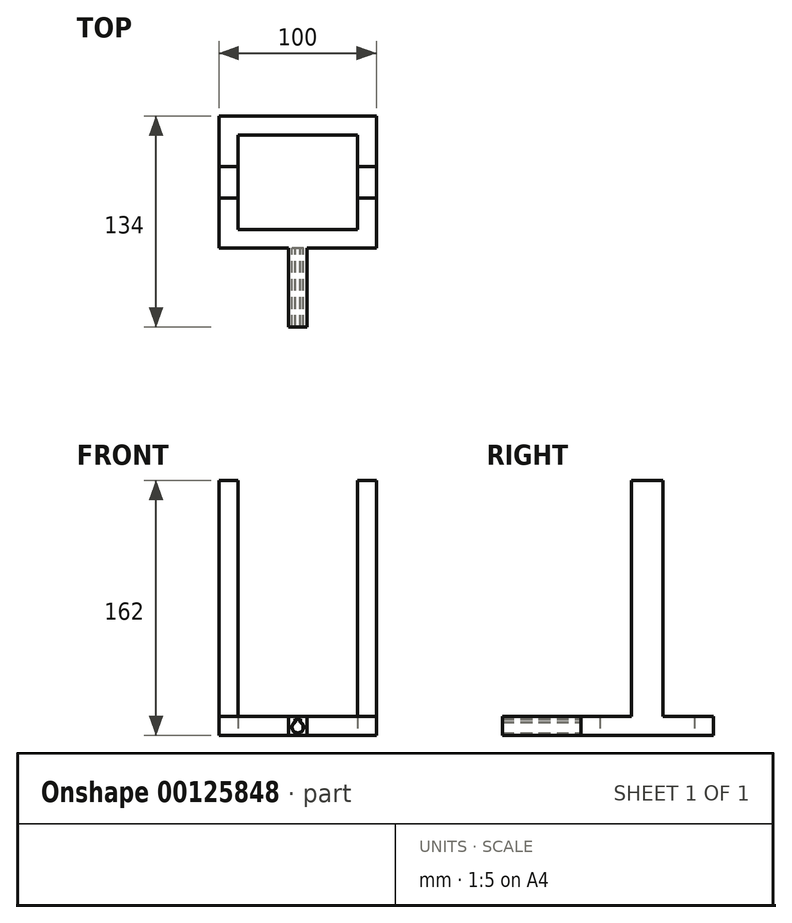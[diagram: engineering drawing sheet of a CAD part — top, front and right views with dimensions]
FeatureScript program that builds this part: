
annotation { "Feature Type Name" : "Feature", "Feature Type Description" : "" }
export const myFeature = defineFeature(function(context is Context, id is Id, definition is map)
    precondition{}
    {
        {
            var Q0;
            Q0=qCreatedBy(makeId("Front.planeOp"),FACE);
            var sketch = newSketch(context, id + "F12", { "sketchPlane" : qUnion([Q0])});
            skCircle(sketch, "E0", {"center": v(0, 0) * mm, "radius": 3.5 * mm});
            skPoint(sketch, "E1", {"position": v(0, 3.5) * mm});
            skSolve(sketch);
        }
        {
            var Q0;
            Q0=makeQuery(id+"F12.imprint","IMPRINT",FACE,{"disambiguationData":[TD([[makeQuery(id+"F12.imprint","IMPRINT",EDGE,{"derivedFrom":sQuery(id+"F12.wireOp",EDGE,"E0")}),1.0]])]});
            extrude(context, id + "F0", {"entities" : qUnion([Q0]), "depth" : 50 * mm});
        }
        {
            var Q0;
            Q0=qCreatedBy(makeId("Front.planeOp"),FACE);
            var sketch = newSketch(context, id + "F13", { "sketchPlane" : qUnion([Q0])});
            skPoint(sketch, "E2", {"position": v(0, 3.5) * mm});
            skLineSegment(sketch, "E3.bottom", {"start": v(1.5, 5) * mm, "end": v(-1.5, 5) * mm});
            skLineSegment(sketch, "E3.top", {"start": v(1.5, 2) * mm, "end": v(-1.5, 2) * mm});
            skLineSegment(sketch, "E3.left", {"start": v(1.5, 5) * mm, "end": v(1.5, 2) * mm});
            skLineSegment(sketch, "E3.right", {"start": v(-1.5, 5) * mm, "end": v(-1.5, 2) * mm});
            skSolve(sketch);
        }
        {
            var Q0;
            Q0=qSketchRegion(id+"F13",true);
            extrude(context, id + "F1", {"entities" : qUnion([Q0]), "operationType" : NewBodyOperationType.ADD, "depth" : 50 * mm});
        }
        {
            var Q0;
            Q0=makeQuery(id+"F1.boolean.opBoolean","MERGE",FACE,{"derivedFrom":[makeQuery(id+"F0.opExtrude","CAP_FACE",FACE,{"disambiguationData":[OSD([sQuery(id+"F12.wireOp",EDGE,"E0")])],"isStart":false}),makeQuery(id+"F1.opExtrude","CAP_FACE",FACE,{"disambiguationData":[OSD([sQuery(id+"F13.wireOp",EDGE,"E3.bottom"),sQuery(id+"F13.wireOp",EDGE,"E3.top"),sQuery(id+"F13.wireOp",EDGE,"E3.left"),sQuery(id+"F13.wireOp",EDGE,"E3.right")])],"isStart":false})]});
            var sketch = newSketch(context, id + "F14", { "sketchPlane" : qUnion([Q0])});
            skPoint(sketch, "E4", {"position": v(0, -3.5) * mm});
            skPoint(sketch, "E5", {"position": v(0, 5) * mm});
            skPoint(sketch, "E6", {"position": v(0, 0.75) * mm});
            skSolve(sketch);
        }
        {
            var Q0;
            Q0=qCreatedBy(makeId("Front.planeOp"),FACE);
            var sketch = newSketch(context, id + "F15", { "sketchPlane" : qUnion([Q0])});
            skPoint(sketch, "E7", {"position": v(0, 0.75) * mm});
            skLineSegment(sketch, "E8.bottom", {"start": v(6, -5.25) * mm, "end": v(-6, -5.25) * mm});
            skLineSegment(sketch, "E8.top", {"start": v(6, 6.75) * mm, "end": v(-6, 6.75) * mm});
            skLineSegment(sketch, "E8.left", {"start": v(6, -5.25) * mm, "end": v(6, 6.75) * mm});
            skLineSegment(sketch, "E8.right", {"start": v(-6, -5.25) * mm, "end": v(-6, 6.75) * mm});
            skSolve(sketch);
        }
        {
            var Q0;
            Q0=qSketchRegion(id+"F15",true);
            extrude(context, id + "F2", {"entities" : qUnion([Q0]), "depth" : 50 * mm});
        }
        {
            var Q0;
            Q0=makeQuery(id+"F0.opExtrude","SWEPT_BODY",BODY,{"disambiguationData":[OSD([sQuery(id+"F12.wireOp",EDGE,"E0")])]});
            var Q1;
            Q1=makeQuery(id+"F2.opExtrude","SWEPT_BODY",BODY,{"disambiguationData":[OSD([sQuery(id+"F15.wireOp",EDGE,"E8.bottom"),sQuery(id+"F15.wireOp",EDGE,"E8.top"),sQuery(id+"F15.wireOp",EDGE,"E8.left"),sQuery(id+"F15.wireOp",EDGE,"E8.right")])]});
            booleanBodies(context, id + "F3", {"operationType" : BooleanOperationType.SUBTRACTION, "tools" : qUnion([Q0]), "targets" : qUnion([Q1]), "offset" : true, "offsetAll" : true, "offsetDistance" : 0.25 * mm, "keepTools" : true});
        }
        {
            var Q0;
            Q0=makeQuery(id+"F2.opExtrude","CAP_FACE",FACE,{"disambiguationData":[OSD([sQuery(id+"F15.wireOp",EDGE,"E8.bottom"),sQuery(id+"F15.wireOp",EDGE,"E8.top"),sQuery(id+"F15.wireOp",EDGE,"E8.left"),sQuery(id+"F15.wireOp",EDGE,"E8.right")])],"isStart":true});
            var sketch = newSketch(context, id + "F4", { "sketchPlane" : qUnion([Q0])});
            skPoint(sketch, "E9", {"position": v(6, 0.75) * mm});
            skPoint(sketch, "E10", {"position": v(-6, 0.75) * mm});
            skPoint(sketch, "E11", {"position": v(0, -5.25) * mm});
            skPoint(sketch, "E12", {"position": v(0, 6.75) * mm});
            skLineSegment(sketch, "E13.bottom", {"start": v(-50, 6.75) * mm, "end": v(50, 6.75) * mm});
            skLineSegment(sketch, "E13.top", {"start": v(-50, -5.25) * mm, "end": v(50, -5.25) * mm});
            skLineSegment(sketch, "E13.left", {"start": v(-50, 6.75) * mm, "end": v(-50, -5.25) * mm});
            skLineSegment(sketch, "E13.right", {"start": v(50, 6.75) * mm, "end": v(50, -5.25) * mm});
            skSolve(sketch);
        }
        {
            var Q0;
            Q0=qSketchRegion(id+"F4",true);
            extrude(context, id + "F16", {"entities" : qUnion([Q0]), "operationType" : NewBodyOperationType.ADD, "depth" : 12 * mm});
        }
        {
            var Q0;
            Q0=makeQuery(id+"F16.opExtrude","CAP_FACE",FACE,{"disambiguationData":[OSD([sQuery(id+"F4.wireOp",EDGE,"E13.bottom"),sQuery(id+"F4.wireOp",EDGE,"E13.top"),sQuery(id+"F4.wireOp",EDGE,"E13.left"),sQuery(id+"F4.wireOp",EDGE,"E13.right")])],"isStart":false});
            var sketch = newSketch(context, id + "F5", { "sketchPlane" : qUnion([Q0])});
            skLineSegment(sketch, "E14.bottom", {"start": v(-50, 6.75) * mm, "end": v(-38, 6.75) * mm});
            skLineSegment(sketch, "E14.top", {"start": v(-50, -5.25) * mm, "end": v(-38, -5.25) * mm});
            skLineSegment(sketch, "E14.left", {"start": v(-50, 6.75) * mm, "end": v(-50, -5.25) * mm});
            skLineSegment(sketch, "E14.right", {"start": v(-38, 6.75) * mm, "end": v(-38, -5.25) * mm});
            skSolve(sketch);
        }
        {
            var Q0;
            Q0=qSketchRegion(id+"F5",true);
            extrude(context, id + "F17", {"entities" : qUnion([Q0]), "operationType" : NewBodyOperationType.ADD, "depth" : 72 * mm});
        }
        {
            var Q0;
            Q0=makeQuery(id+"F16.opExtrude","CAP_FACE",FACE,{"disambiguationData":[OSD([sQuery(id+"F4.wireOp",EDGE,"E13.bottom"),sQuery(id+"F4.wireOp",EDGE,"E13.top"),sQuery(id+"F4.wireOp",EDGE,"E13.left"),sQuery(id+"F4.wireOp",EDGE,"E13.right")])],"isStart":false});
            var sketch = newSketch(context, id + "F6", { "sketchPlane" : qUnion([Q0])});
            skLineSegment(sketch, "E15.bottom", {"start": v(50, 6.75) * mm, "end": v(38, 6.75) * mm});
            skLineSegment(sketch, "E15.top", {"start": v(50, -5.25) * mm, "end": v(38, -5.25) * mm});
            skLineSegment(sketch, "E15.left", {"start": v(50, 6.75) * mm, "end": v(50, -5.25) * mm});
            skLineSegment(sketch, "E15.right", {"start": v(38, 6.75) * mm, "end": v(38, -5.25) * mm});
            skSolve(sketch);
        }
        {
            var Q0;
            Q0=makeQuery(id+"F6.imprint","IMPRINT",FACE,{"disambiguationData":[TD([[makeQuery(id+"F6.imprint","IMPRINT",EDGE,{"derivedFrom":sQuery(id+"F6.wireOp",EDGE,"E15.bottom")}),-1.0]])]});
            extrude(context, id + "F7", {"entities" : qUnion([Q0]), "operationType" : NewBodyOperationType.ADD, "depth" : 72 * mm});
        }
        {
            var Q0;
            Q0=makeQuery(id+"F17.opExtrude","SWEPT_FACE",FACE,{"disambiguationData":[OSD([sQuery(id+"F5.wireOp",EDGE,"E14.right")])]});
            var sketch = newSketch(context, id + "F18", { "sketchPlane" : qUnion([Q0])});
            skLineSegment(sketch, "E16.bottom", {"start": v(-84, 6.75) * mm, "end": v(-72, 6.75) * mm});
            skLineSegment(sketch, "E16.top", {"start": v(-84, -5.25) * mm, "end": v(-72, -5.25) * mm});
            skLineSegment(sketch, "E16.left", {"start": v(-84, 6.75) * mm, "end": v(-84, -5.25) * mm});
            skLineSegment(sketch, "E16.right", {"start": v(-72, 6.75) * mm, "end": v(-72, -5.25) * mm});
            skSolve(sketch);
        }
        {
            var Q0;
            Q0=qSketchRegion(id+"F18",true);
            extrude(context, id + "F8", {"entities" : qUnion([Q0]), "operationType" : NewBodyOperationType.ADD, "endBound" : BoundingType.UP_TO_NEXT, "depth" : 25 * mm});
        }
        {
            var Q0;
            Q0=makeQuery(id+"F8.boolean.opBoolean","MERGE",FACE,{"derivedFrom":[makeQuery(id+"F7.boolean.opBoolean","MERGE",FACE,{"derivedFrom":[makeQuery(id+"F17.boolean.opBoolean","MERGE",FACE,{"derivedFrom":[makeQuery(id+"F16.boolean.opBoolean","MERGE",FACE,{"derivedFrom":[makeQuery(id+"F2.opExtrude","SWEPT_FACE",FACE,{"disambiguationData":[OSD([sQuery(id+"F15.wireOp",EDGE,"E8.top")])]}),makeQuery(id+"F16.opExtrude","SWEPT_FACE",FACE,{"disambiguationData":[OSD([sQuery(id+"F4.wireOp",EDGE,"E13.bottom")])]})]}),makeQuery(id+"F17.opExtrude","SWEPT_FACE",FACE,{"disambiguationData":[OSD([sQuery(id+"F5.wireOp",EDGE,"E14.bottom")])]})]}),makeQuery(id+"F7.opExtrude","SWEPT_FACE",FACE,{"disambiguationData":[OSD([sQuery(id+"F6.wireOp",EDGE,"E15.bottom")])]})]}),makeQuery(id+"F8.opExtrude","SWEPT_FACE",FACE,{"disambiguationData":[OSD([sQuery(id+"F18.wireOp",EDGE,"E16.bottom")])]})]});
            var sketch = newSketch(context, id + "F9", { "sketchPlane" : qUnion([Q0])});
            skPoint(sketch, "E17", {"position": v(-50, 42) * mm});
            skPoint(sketch, "E18", {"position": v(-38, 42) * mm});
            skPoint(sketch, "E19", {"position": v(38, 42) * mm});
            skPoint(sketch, "E20", {"position": v(50, 42) * mm});
            skPoint(sketch, "E21", {"position": v(44, 42) * mm});
            skPoint(sketch, "E22", {"position": v(-44, 42) * mm});
            skLineSegment(sketch, "E23.bottom", {"start": v(-38, 32) * mm, "end": v(-50, 32) * mm});
            skLineSegment(sketch, "E23.top", {"start": v(-38, 52) * mm, "end": v(-50, 52) * mm});
            skLineSegment(sketch, "E23.left", {"start": v(-38, 32) * mm, "end": v(-38, 52) * mm});
            skLineSegment(sketch, "E23.right", {"start": v(-50, 32) * mm, "end": v(-50, 52) * mm});
            skLineSegment(sketch, "E24.bottom", {"start": v(-38, 32) * mm, "end": v(-38, 32) * mm});
            skLineSegment(sketch, "E24.top", {"start": v(-38, 32) * mm, "end": v(-38, 32) * mm});
            skLineSegment(sketch, "E24.left", {"start": v(-38, 32) * mm, "end": v(-38, 32) * mm});
            skLineSegment(sketch, "E24.right", {"start": v(-38, 32) * mm, "end": v(-38, 32) * mm});
            skPoint(sketch, "E24.middle", {"position": v(-38, 32) * mm});
            skLineSegment(sketch, "E25.bottom", {"start": v(50, 32) * mm, "end": v(38, 32) * mm});
            skLineSegment(sketch, "E25.top", {"start": v(50, 52) * mm, "end": v(38, 52) * mm});
            skLineSegment(sketch, "E25.left", {"start": v(50, 32) * mm, "end": v(50, 52) * mm});
            skLineSegment(sketch, "E25.right", {"start": v(38, 32) * mm, "end": v(38, 52) * mm});
            skSolve(sketch);
        }
        {
            var Q0;
            Q0=qSketchRegion(id+"F9",true);
            extrude(context, id + "F10", {"entities" : qUnion([Q0]), "operationType" : NewBodyOperationType.ADD, "depth" : 150 * mm});
        }
    });
